# Revit family: FF70
name_source: partatom
category: 门
units: mm (PartAtom-declared; Revit-internal decimal feet)

## family parameters
主体 = 墙
共享 = 否
加载时剪切的空心 = 否
总是垂直 = 是
房间计算点 = 否

## types (9) — shared parameters
Height above ground = 4' - 0"
Width of Switch = 1' - 0"
depth of Switch = 0' - 5"
height of Switch = 1' - 4"
分析构造 = <无>
定义热属性方式 = 示意图类型
默认高程 = 0' - 0"

## per-type parameters (varying)
| type | LAVOUT B | LAYOUT A | LAYOUT C | LAYOUT D | LAYOUT E | LAYOUT F | LAYOUT G | LAYOUT H | LAYOUT J |
| LAYOUT H | 否 | 否 | 否 | 否 | 否 | 否 | 否 | 是 | 否 |
| LAYOUT G | 否 | 否 | 否 | 否 | 否 | 否 | 是 | 否 | 否 |
| LAYOUT A | 否 | 是 | 否 | 否 | 否 | 否 | 否 | 否 | 否 |
| LAYOUT F | 否 | 否 | 否 | 否 | 否 | 是 | 否 | 否 | 否 |
| LAYOUT B | 是 | 否 | 否 | 否 | 否 | 否 | 否 | 否 | 否 |
| LAYOUT C | 否 | 否 | 是 | 否 | 否 | 否 | 否 | 否 | 否 |
| LAYOUT D | 否 | 否 | 否 | 是 | 否 | 否 | 否 | 否 | 否 |
| LAYOUT E | 否 | 否 | 否 | 否 | 是 | 否 | 否 | 否 | 否 |
| LAYOUT J | 否 | 否 | 否 | 否 | 否 | 否 | 否 | 否 | 是 |

## geometry (parser evidence)
native form markers: Blend x12, Sweep x96
no freeform markers — native parametric forms only
